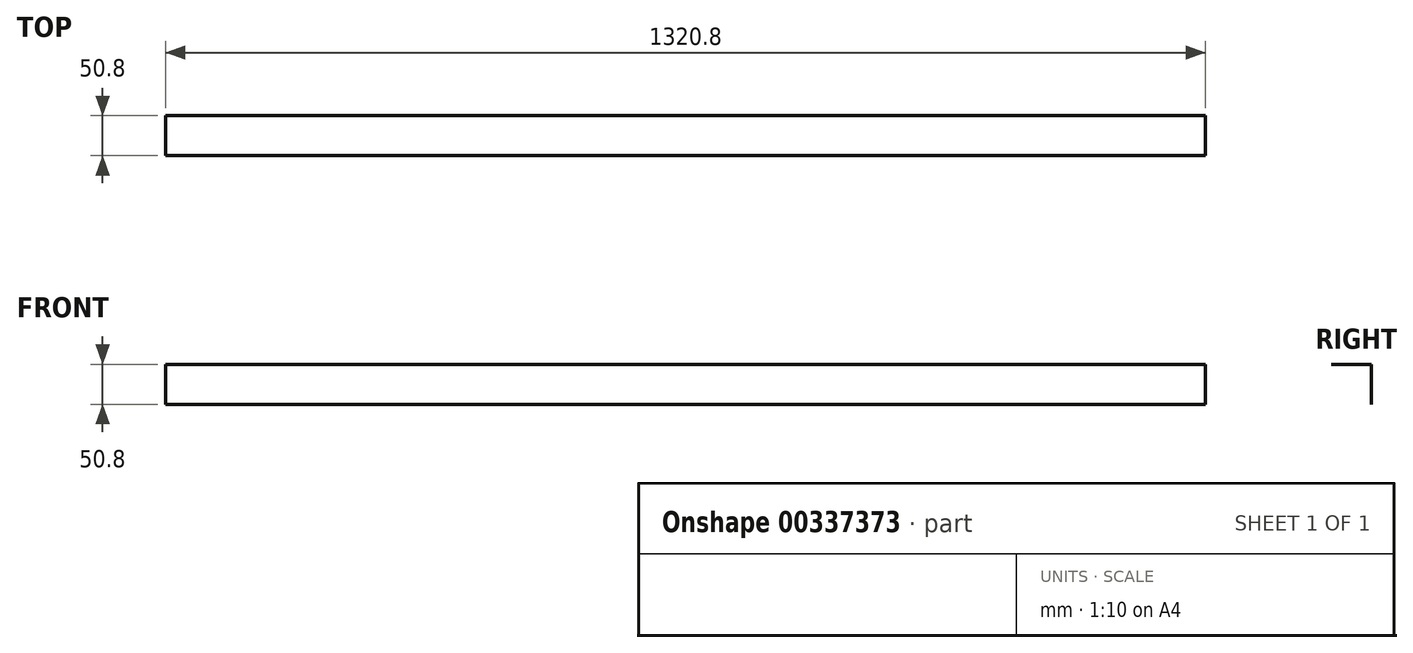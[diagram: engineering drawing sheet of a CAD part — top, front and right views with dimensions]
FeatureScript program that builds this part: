
annotation { "Feature Type Name" : "Feature", "Feature Type Description" : "" }
export const myFeature = defineFeature(function(context is Context, id is Id, definition is map)
    precondition{}
    {
        {
            var Q0;
            Q0=qCreatedBy(makeId("Right.planeOp"),FACE);
            var sketch = newSketch(context, id + "F0", { "sketchPlane" : qUnion([Q0])});
            skLineSegment(sketch, "E0", {"start": v(-24.83, -48.84) * mm, "end": v(-24.83, 1.96) * mm});
            skLineSegment(sketch, "E1", {"start": v(-24.83, 1.96) * mm, "end": v(-75.63, 1.96) * mm});
            skSolve(sketch);
        }
        {
            var Q0;
            Q0 = qSketchRegion(id + "F0", true);
            var Q1;
            Q1=sQuery(id+"F0.wireOp",EDGE,"E1");
            var Q2;
            Q2=sQuery(id+"F0.wireOp",EDGE,"E0");
            extrude(context, id + "F1", {"entities" : qUnion([Q0]), "bodyType" : ToolBodyType.SURFACE, "surfaceEntities" : qUnion([Q1, Q2]), "depth" : 1320.8 * mm});
        }
    });
